# Revit family: PIA-200_RFA
name_source: partatom
category: Aparatos sanitarios
units: mm (PartAtom-declared; Revit-internal decimal feet)

## family parameters
Compartido = Sí
Corte con vacíos al cargar = No
Cota de conector redondo = Diámetro de uso
Número OmniClass = 23.45.55.14
Punto de cálculo de habitación = Sí
Se basa en plano de trabajo = Sí
Siempre vertical = Sí
Tipo de pieza = Normal
Título OmniClass = Single Faucets

## types (1)
- E-714
    Brass Chromed = Brass
    Cartucho = Cartucho de 35 mm
    Comentarios de tipo = Monomando para Regadera o Tina sin Desviador
    Descripción = Monomando para Regadera o Tina sin Desviador
    Elevación por defecto = 1"
    Fabricante = HELVEX S.A. DE C.V.
    Garantía = El producto HELVEX está garantizado como libre
de defectos en materiales y procesos de
fabricación.
El producto HELVEX está garantizado, en lo que
se refiere a los acabados; por un periodo de 10
años en los acabados cromo y duravex, y por 2
años en cabados diferentes al cromo, a partir de
la fecha de compra indicada en la factura.
    Imagen de tipo = E-714.jpg
    Instalación = ½" - 14 NPT
    Modelo = E-714
    Operación = Para abrir el flujo de agua levante la palanca maneral y gire para regular la temperatura.
    Presión máxima de trabajo = 85.3 psi
    Presión mínima de trabajo = 14.2 psi
    Support Base Diameter = 4"
    Total Height = 7"

## geometry (parser evidence)
native form markers: Sweep x3
no freeform markers — native parametric forms only
